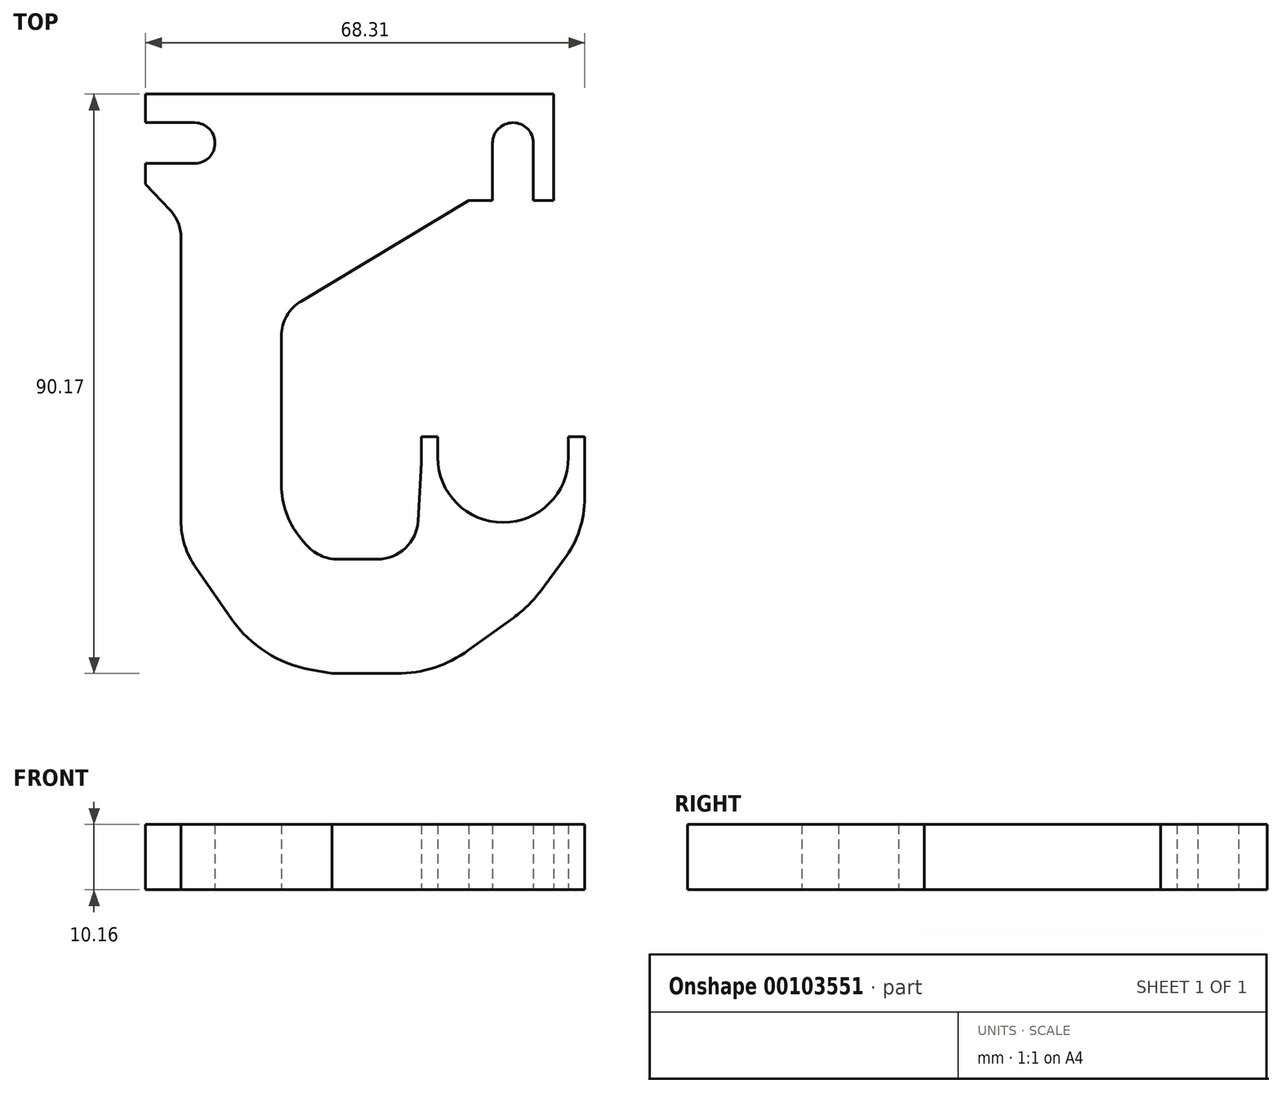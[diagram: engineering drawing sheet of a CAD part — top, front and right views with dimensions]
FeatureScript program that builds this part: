
annotation { "Feature Type Name" : "Feature", "Feature Type Description" : "" }
export const myFeature = defineFeature(function(context is Context, id is Id, definition is map)
    precondition{}
    {
        {
            var Q0;
            Q0=qCreatedBy(makeId("Top.planeOp"),FACE);
            var sketch = newSketch(context, id + "F0", { "sketchPlane" : qUnion([Q0])});
            skLineSegment(sketch, "E0", {"start": v(-45.22, 27.54) * mm, "end": v(18.28, 27.54) * mm});
            skLineSegment(sketch, "E1", {"start": v(18.28, 27.54) * mm, "end": v(18.28, 23.8) * mm});
            skLineSegment(sketch, "E2", {"start": v(18.28, 10.97) * mm, "end": v(15.1, 10.97) * mm});
            skLineSegment(sketch, "E3", {"start": v(5.06, 10.97) * mm, "end": v(-21.02, -4.68) * mm});
            skLineSegment(sketch, "E4", {"start": v(-24.1, -10.13) * mm, "end": v(-24.1, -33.35) * mm});
            skLineSegment(sketch, "E5", {"start": v(-21.22, -41.4) * mm, "end": v(-20.33, -42.48) * mm});
            skLineSegment(sketch, "E6", {"start": v(-15.33, -44.85) * mm, "end": v(-9.16, -44.85) * mm});
            skLineSegment(sketch, "E7", {"start": v(-2.82, -38.86) * mm, "end": v(-2.3, -29.82) * mm});
            skLineSegment(sketch, "E8", {"start": v(-2.3, -29.82) * mm, "end": v(-2.3, -25.8) * mm});
            skLineSegment(sketch, "E9", {"start": v(-2.3, -25.8) * mm, "end": v(0.23, -25.8) * mm});
            skLineSegment(sketch, "E10", {"start": v(23.1, -25.8) * mm, "end": v(23.1, -35.24) * mm});
            skLineSegment(sketch, "E11", {"start": v(19.87, -44.91) * mm, "end": v(16.15, -49.88) * mm});
            skLineSegment(sketch, "E12", {"start": v(12.07, -53.9) * mm, "end": v(5, -59.01) * mm});
            skLineSegment(sketch, "E13", {"start": v(-6.17, -62.63) * mm, "end": v(-16.23, -62.63) * mm});
            skLineSegment(sketch, "E14", {"start": v(-16.23, -62.63) * mm, "end": v(-19.55, -62.04) * mm});
            skLineSegment(sketch, "E15", {"start": v(-31.82, -54.18) * mm, "end": v(-37.43, -46.13) * mm});
            skLineSegment(sketch, "E16", {"start": v(-39.71, -38.86) * mm, "end": v(-39.71, -11.94) * mm});
            skLineSegment(sketch, "E17", {"start": v(-39.71, -11.94) * mm, "end": v(-39.71, 0) * mm});
            skLineSegment(sketch, "E18", {"start": v(-39.71, 0) * mm, "end": v(-39.71, 5.18) * mm});
            skLineSegment(sketch, "E19", {"start": v(-41.45, 9.55) * mm, "end": v(-45.22, 13.52) * mm});
            skLineSegment(sketch, "E20", {"start": v(-45.22, 13.52) * mm, "end": v(-45.22, 16.74) * mm});
            skLineSegment(sketch, "E21.trimOffspring", {"start": v(18.28, 27.54) * mm, "end": v(18.28, 10.97) * mm});
            skLineSegment(sketch, "E22", {"start": v(-45.22, 23.1) * mm, "end": v(-37.6, 23.1) * mm});
            skLineSegment(sketch, "E23", {"start": v(-37.6, 16.74) * mm, "end": v(-45.22, 16.74) * mm});
            skLineSegment(sketch, "E24.trimOffspring", {"start": v(-45.22, 23.1) * mm, "end": v(-45.22, 27.54) * mm});
            skArc(sketch, "E25", {"start": v(-37.6, 16.74) * mm, "mid": v(-34.42, 19.92) * mm, "end": v(-37.6, 23.1) * mm});
            skLineSegment(sketch, "E26", {"start": v(15.1, 10.97) * mm, "end": v(15.1, 19.92) * mm});
            skLineSegment(sketch, "E27", {"start": v(8.76, 19.92) * mm, "end": v(8.76, 10.97) * mm});
            skLineSegment(sketch, "E28.trimOffspring", {"start": v(8.76, 10.97) * mm, "end": v(5.06, 10.97) * mm});
            skArc(sketch, "E29", {"start": v(15.1, 19.92) * mm, "mid": v(11.93, 23.1) * mm, "end": v(8.76, 19.92) * mm});
            skLineSegment(sketch, "E30", {"start": v(0.23, -25.8) * mm, "end": v(0.23, -28.98) * mm});
            skLineSegment(sketch, "E31", {"start": v(20.55, -28.98) * mm, "end": v(20.55, -25.8) * mm});
            skArc(sketch, "E32", {"start": v(0.23, -28.98) * mm, "mid": v(10.4, -39.14) * mm, "end": v(20.55, -28.98) * mm});
            skLineSegment(sketch, "E33.trimOffspring", {"start": v(20.55, -25.8) * mm, "end": v(23.1, -25.8) * mm});
            skPoint(sketch, "E34.visualSharp", {"position": v(-39.71, -42.85) * mm});
            skArc(sketch, "E34.filletArc", {"start": v(-39.71, -38.86) * mm, "mid": v(-39.13, -42.67) * mm, "end": v(-37.43, -46.13) * mm});
            skPoint(sketch, "E35.visualSharp", {"position": v(-27.3, -60.65) * mm});
            skArc(sketch, "E35.filletArc", {"start": v(-31.82, -54.18) * mm, "mid": v(-26.46, -59.33) * mm, "end": v(-19.55, -62.04) * mm});
            skPoint(sketch, "E36.visualSharp", {"position": v(-3.15, -44.85) * mm});
            skArc(sketch, "E36.filletArc", {"start": v(-9.16, -44.85) * mm, "mid": v(-4.8, -43.12) * mm, "end": v(-2.82, -38.86) * mm});
            skPoint(sketch, "E37.visualSharp", {"position": v(-24.1, -37.89) * mm});
            skArc(sketch, "E37.filletArc", {"start": v(-24.1, -33.35) * mm, "mid": v(-23.36, -37.62) * mm, "end": v(-21.22, -41.4) * mm});
            skPoint(sketch, "E38.visualSharp", {"position": v(-18.39, -44.85) * mm});
            skArc(sketch, "E38.filletArc", {"start": v(-20.33, -42.48) * mm, "mid": v(-18.1, -44.23) * mm, "end": v(-15.33, -44.85) * mm});
            skPoint(sketch, "E39.visualSharp", {"position": v(-24.1, -6.53) * mm});
            skArc(sketch, "E39.filletArc", {"start": v(-21.02, -4.68) * mm, "mid": v(-23.27, -7) * mm, "end": v(-24.1, -10.13) * mm});
            skPoint(sketch, "E40.visualSharp", {"position": v(0, -62.63) * mm});
            skArc(sketch, "E40.filletArc", {"start": v(-6.17, -62.63) * mm, "mid": v(-0.3, -61.7) * mm, "end": v(5, -59.01) * mm});
            skArc(sketch, "E41.filletArc", {"start": v(12.07, -53.9) * mm, "mid": v(14.26, -52.04) * mm, "end": v(16.15, -49.88) * mm});
            skArc(sketch, "E42.filletArc", {"start": v(19.87, -44.91) * mm, "mid": v(22.27, -40.34) * mm, "end": v(23.1, -35.24) * mm});
            skPoint(sketch, "E43.visualSharp", {"position": v(-39.71, 7.7) * mm});
            skArc(sketch, "E43.filletArc", {"start": v(-39.71, 5.18) * mm, "mid": v(-40.16, 7.53) * mm, "end": v(-41.45, 9.55) * mm});
            skSolve(sketch);
        }
        {
            var Q0;
            {var subQ1=sQuery(id+"F0.wireOp",EDGE,"E0");Q0=makeQuery(id+"F0.imprint","IMPRINT",FACE,{"disambiguationData":[TD([[makeQuery(id+"F0.imprint","IMPRINT",EDGE,{"derivedFrom":subQ1}),-1.0]])]});}
            extrude(context, id + "F1", {"entities" : qUnion([Q0]), "offsetDistance" : 25.4 * mm, "depth" : 10.16 * mm});
        }
    });
